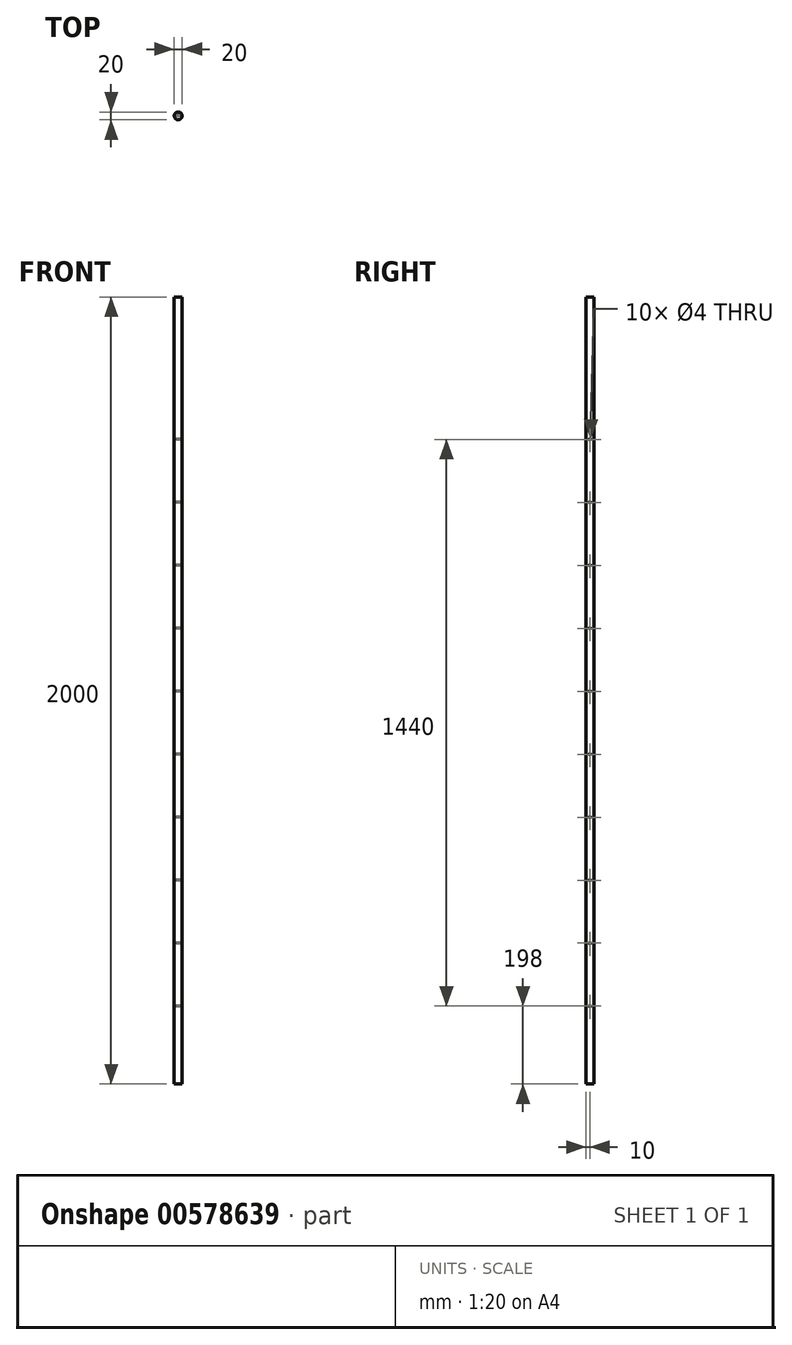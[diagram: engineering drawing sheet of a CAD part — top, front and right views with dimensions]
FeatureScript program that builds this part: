
annotation { "Feature Type Name" : "Feature", "Feature Type Description" : "" }
export const myFeature = defineFeature(function(context is Context, id is Id, definition is map)
    precondition{}
    {
        {
            var Q0;
            Q0=qCreatedBy(makeId("Top.planeOp"),FACE);
            var sketch = newSketch(context, id + "F0", { "sketchPlane" : qUnion([Q0])});
            skCircle(sketch, "E0", {"center": v(0, 0) * mm, "radius": 10 * mm});
            skSolve(sketch);
        }
        {
            var Q0;
            Q0 = qSketchRegion(id + "F0", true);
            extrude(context, id + "F1", {"entities" : qUnion([Q0]), "flatOperationType" : FlatOperationType.REMOVE, "depth" : 2000 * mm, "offsetDistance" : 25 * mm, "domain" : OperationDomain.MODEL});
        }
        {
            var Q0;
            Q0=qCreatedBy(makeId("Right.planeOp"),FACE);
            var sketch = newSketch(context, id + "F2", { "sketchPlane" : qUnion([Q0])});
            skPoint(sketch, "E1", {"position": v(0, 198) * mm});
            skCircle(sketch, "E2", {"center": v(0, 198) * mm, "radius": 2 * mm});
            skCircle(sketch, "E3.1.0.0", {"center": v(0, 358) * mm, "radius": 2 * mm});
            skPoint(sketch, "E3.1.0.1", {"position": v(0, 358) * mm});
            skCircle(sketch, "E3.2.0.0", {"center": v(0, 518) * mm, "radius": 2 * mm});
            skPoint(sketch, "E3.2.0.1", {"position": v(0, 518) * mm});
            skLineSegment(sketch, "E3.direction1", {"start": v(0, 198) * mm, "end": v(0, 358) * mm, "construction": true});
            skCircle(sketch, "E4.0.3.0", {"center": v(0, 678) * mm, "radius": 2 * mm});
            skPoint(sketch, "E4.2.3.0", {"position": v(0, 678) * mm});
            skCircle(sketch, "E4.0.4.0", {"center": v(0, 838) * mm, "radius": 2 * mm});
            skPoint(sketch, "E4.2.4.0", {"position": v(0, 838) * mm});
            skCircle(sketch, "E4.0.5.0", {"center": v(0, 998) * mm, "radius": 2 * mm});
            skPoint(sketch, "E4.2.5.0", {"position": v(0, 998) * mm});
            skCircle(sketch, "E4.0.6.0", {"center": v(0, 1158) * mm, "radius": 2 * mm});
            skPoint(sketch, "E4.2.6.0", {"position": v(0, 1158) * mm});
            skCircle(sketch, "E4.0.7.0", {"center": v(0, 1318) * mm, "radius": 2 * mm});
            skPoint(sketch, "E4.2.7.0", {"position": v(0, 1318) * mm});
            skCircle(sketch, "E4.0.8.0", {"center": v(0, 1478) * mm, "radius": 2 * mm});
            skPoint(sketch, "E4.2.8.0", {"position": v(0, 1478) * mm});
            skCircle(sketch, "E4.0.9.0", {"center": v(0, 1638) * mm, "radius": 2 * mm});
            skPoint(sketch, "E4.2.9.0", {"position": v(0, 1638) * mm});
            skSolve(sketch);
        }
        {
            var Q0;
            Q0 = qSketchRegion(id + "F2", true);
            extrude(context, id + "F3", {"entities" : qUnion([Q0]), "operationType" : NewBodyOperationType.REMOVE, "depth" : 25 * mm, "offsetDistance" : 25 * mm, "symmetric" : true});
        }
    });
